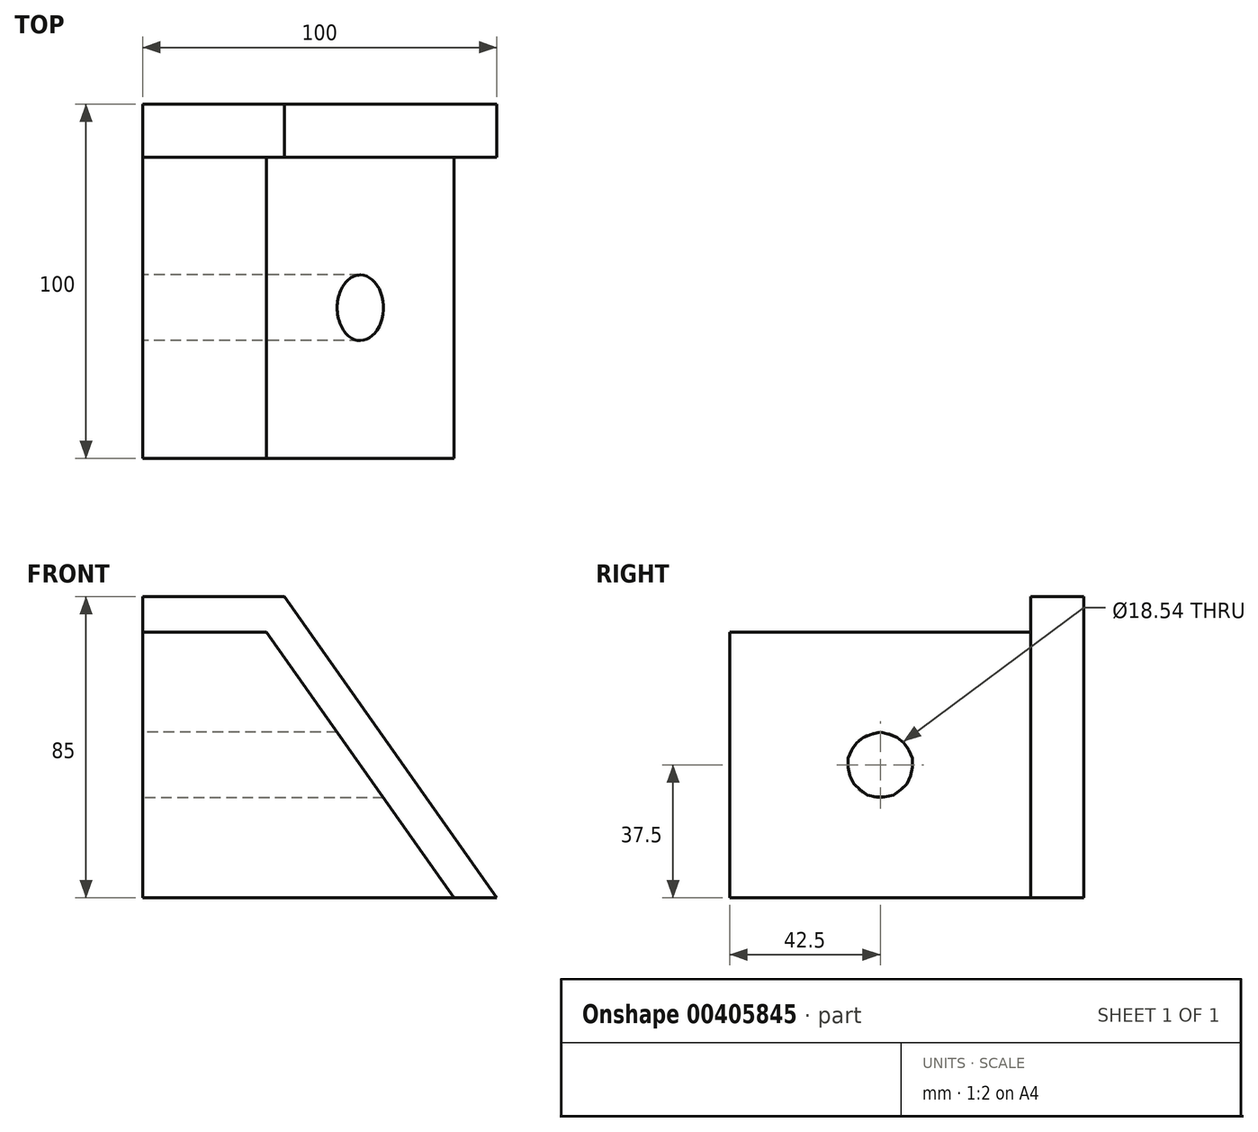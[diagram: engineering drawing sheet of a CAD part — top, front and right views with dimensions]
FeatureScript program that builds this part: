
annotation { "Feature Type Name" : "Feature", "Feature Type Description" : "" }
export const myFeature = defineFeature(function(context is Context, id is Id, definition is map)
    precondition{}
    {
        {
            var Q0;
            Q0=qCreatedBy(makeId("Front.planeOp"),FACE);
            var sketch = newSketch(context, id + "F0", { "sketchPlane" : qUnion([Q0])});
            skLineSegment(sketch, "E0.bottom", {"start": v(0, 0) * mm, "end": v(-100, 0) * mm});
            skLineSegment(sketch, "E0.top", {"start": v(0, 85) * mm, "end": v(-100, 85) * mm});
            skLineSegment(sketch, "E0.left", {"start": v(0, 0) * mm, "end": v(0, 85) * mm});
            skLineSegment(sketch, "E0.right", {"start": v(-100, 0) * mm, "end": v(-100, 85) * mm});
            skLineSegment(sketch, "E1", {"start": v(0, 0) * mm, "end": v(-60, 85) * mm});
            skSolve(sketch);
        }
        {
            var Q0;
            {var subQ1=sQuery(id+"F0.wireOp",EDGE,"E0.bottom");Q0=makeQuery(id+"F0.imprint","IMPRINT",FACE,{"disambiguationData":[TD([[makeQuery(id+"F0.imprint","IMPRINT",EDGE,{"derivedFrom":subQ1}),-1.0]])]});}
            extrude(context, id + "F1", {"entities" : qUnion([Q0]), "depth" : 15 * mm});
        }
        {
            var Q0;
            Q0=makeQuery(id+"F1.opExtrude","CAP_FACE",FACE,{"disambiguationData":[OSD([sQuery(id+"F0.wireOp",EDGE,"E0.bottom"),sQuery(id+"F0.wireOp",EDGE,"E0.top"),sQuery(id+"F0.wireOp",EDGE,"E0.left"),sQuery(id+"F0.wireOp",EDGE,"E0.right"),sQuery(id+"F0.wireOp",EDGE,"IbPc8Rpo-XORN-d5Iq-2zng-wP4s0sQ2uOL1")])],"isStart":false});
            var sketch = newSketch(context, id + "F2", { "sketchPlane" : qUnion([Q0])});
            skLineSegment(sketch, "E2", {"start": v(-100, 75) * mm, "end": v(-65, 75) * mm});
            skLineSegment(sketch, "E3", {"start": v(-65, 75) * mm, "end": v(-12.06, 0) * mm});
            skSolve(sketch);
        }
        {
            var Q0;
            {var subQ0=sQuery(id+"F2.wireOp",EDGE,"E2");Q0=makeQuery(id+"F2.imprint","IMPRINT",FACE,{"disambiguationData":[TD([[makeQuery(id+"F2.imprint","IMPRINT",EDGE,{"derivedFrom":subQ0}),-1.0]])]});}
            extrude(context, id + "F3", {"entities" : qUnion([Q0]), "operationType" : NewBodyOperationType.ADD, "depth" : 85 * mm});
        }
        {
            var Q0;
            {var subQ0=sQuery(id+"F0.wireOp",EDGE,"E0.right");Q0=makeQuery(id+"F3.boolean.opBoolean","MERGE",FACE,{"derivedFrom":[makeQuery(id+"F1.opExtrude","SWEPT_FACE",FACE,{"disambiguationData":[OSD([subQ0])]}),makeQuery(id+"F3.opExtrude","SWEPT_FACE",FACE,{"disambiguationData":[OSD([subQ0])]})]});}
            var sketch = newSketch(context, id + "F4", { "sketchPlane" : qUnion([Q0])});
            skCircle(sketch, "E4", {"center": v(57.5, 37.5) * mm, "radius": 9.27 * mm});
            skPoint(sketch, "E4.centerSnap0", {"position": v(100, 37.5) * mm});
            skPoint(sketch, "E4.centerSnap1", {"position": v(57.5, 75) * mm});
            skSolve(sketch);
        }
        {
            var Q0;
            Q0=makeQuery(id+"F4.imprint","IMPRINT",FACE,{"disambiguationData":[TD([[makeQuery(id+"F4.imprint","IMPRINT",EDGE,{"derivedFrom":sQuery(id+"F4.wireOp",EDGE,"E4")}),1.0]])]});
            extrude(context, id + "F5", {"entities" : qUnion([Q0]), "operationType" : NewBodyOperationType.REMOVE, "endBound" : BoundingType.THROUGH_ALL, "oppositeDirection" : true, "depth" : 25 * mm});
        }
    });
